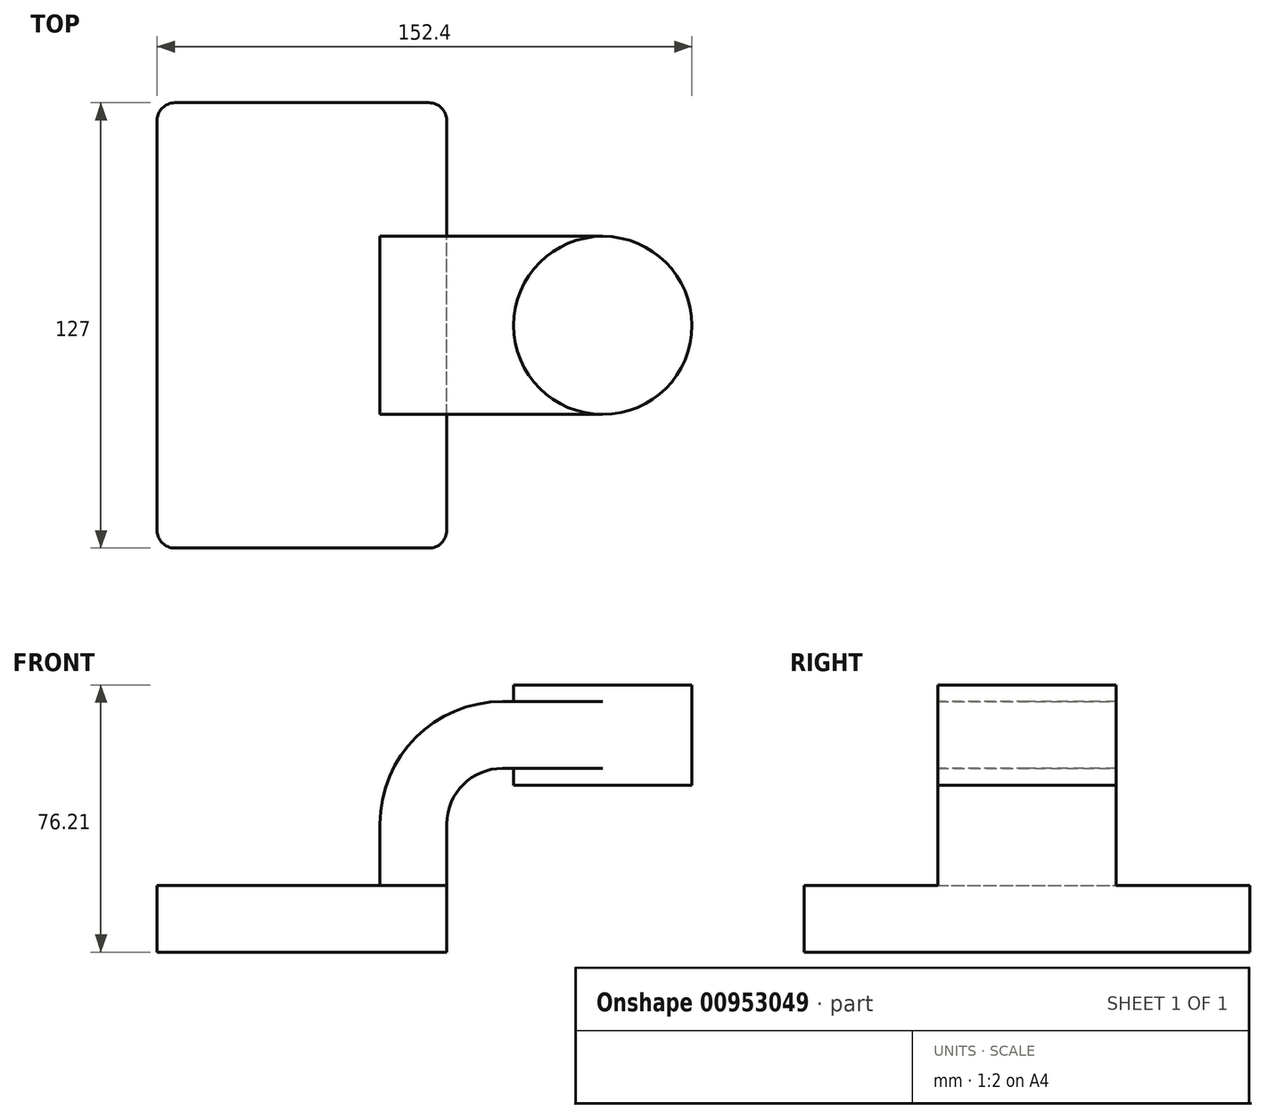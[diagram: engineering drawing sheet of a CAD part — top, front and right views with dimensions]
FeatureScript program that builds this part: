
annotation { "Feature Type Name" : "Feature", "Feature Type Description" : "" }
export const myFeature = defineFeature(function(context is Context, id is Id, definition is map)
    precondition{}
    {
        {
            var Q0;
            Q0=qCreatedBy(makeId("Front.planeOp"),FACE);
            var sketch = newSketch(context, id + "F0", { "sketchPlane" : qUnion([Q0])});
            skLineSegment(sketch, "E0.bottom", {"start": v(-41.28, 9.53) * mm, "end": v(41.28, 9.53) * mm});
            skLineSegment(sketch, "E0.top", {"start": v(-41.28, -9.53) * mm, "end": v(41.28, -9.53) * mm});
            skLineSegment(sketch, "E0.left", {"start": v(-41.28, 9.53) * mm, "end": v(-41.28, -9.53) * mm});
            skLineSegment(sketch, "E0.right", {"start": v(41.27, 9.53) * mm, "end": v(41.28, -9.53) * mm});
            skLineSegment(sketch, "E1.bottom", {"start": v(60.32, 66.68) * mm, "end": v(111.12, 66.68) * mm});
            skLineSegment(sketch, "E1.top", {"start": v(60.32, 38.1) * mm, "end": v(111.12, 38.1) * mm});
            skLineSegment(sketch, "E1.left", {"start": v(60.32, 66.68) * mm, "end": v(60.32, 38.1) * mm});
            skLineSegment(sketch, "E1.right", {"start": v(111.12, 66.68) * mm, "end": v(111.12, 38.1) * mm});
            skPoint(sketch, "E1.middle", {"position": v(85.72, 52.39) * mm});
            skLineSegment(sketch, "E2", {"start": v(41.27, 9.53) * mm, "end": v(41.27, 27) * mm});
            skArc(sketch, "E3", {"start": v(41.28, 27) * mm, "mid": v(45.92, 38.23) * mm, "end": v(57.15, 42.88) * mm});
            skLineSegment(sketch, "E4", {"start": v(57.15, 42.88) * mm, "end": v(85.72, 42.88) * mm});
            skLineSegment(sketch, "E5.0", {"start": v(57.15, 61.93) * mm, "end": v(85.72, 61.93) * mm});
            skArc(sketch, "E5.1", {"start": v(22.23, 27) * mm, "mid": v(32.45, 51.7) * mm, "end": v(57.15, 61.93) * mm});
            skLineSegment(sketch, "E5.2", {"start": v(22.23, 9.53) * mm, "end": v(22.23, 27) * mm});
            skLineSegment(sketch, "E6", {"start": v(85.72, 38.1) * mm, "end": v(85.72, 66.68) * mm});
            skFitSpline(sketch, "E7", {"points": [v(-41.28, 9.53) * mm, v(57.15, 61.93) * mm], "startDerivative": vector(2.38, 87.5) * mm, "endDerivative": vector(125.75, -2.56) * mm});
            skSolve(sketch);
        }
        {
            var Q0;
            Q0=makeQuery(id+"F0.imprint","IMPRINT",FACE,{"disambiguationData":[TD([[makeQuery(id+"F0.imprint","IMPRINT",EDGE,{"derivedFrom":sQuery(id+"F0.wireOp",EDGE,"E0.top")}),1.0]])]});
            extrude(context, id + "F1", {"entities" : qUnion([Q0]), "endBound" : BoundingType.SYMMETRIC, "depth" : 127 * mm, "offsetDistance" : 25.4 * mm});
        }
        {
            var Q0;
            {var subQ1=sQuery(id+"F0.wireOp",EDGE,"E2");Q0=makeQuery(id+"F0.imprint","IMPRINT",FACE,{"disambiguationData":[TD([[makeQuery(id+"F0.imprint","IMPRINT",EDGE,{"derivedFrom":subQ1}),1.0]])]});}
            var Q1;
            {var subQ0=sQuery(id+"F0.wireOp",EDGE,"E5.0");var subQ1=sQuery(id+"F0.wireOp",EDGE,"E1.left");var subQ2=makeQuery(id+"F0.imprint","INTERSECT",VERTEX,{"derivedFrom":[subQ1,subQ0]});Q1=makeQuery(id+"F0.imprint","IMPRINT",FACE,{"disambiguationData":[TD([[makeQuery(id+"F0.imprint","IMPRINT",EDGE,{"disambiguationData":[TD([[subQ2,-1.0]])],"derivedFrom":subQ1}),1.0]])]});}
            extrude(context, id + "F2", {"entities" : qUnion([Q0, Q1]), "operationType" : NewBodyOperationType.ADD, "endBound" : BoundingType.SYMMETRIC, "depth" : 50.8 * mm, "offsetDistance" : 25.4 * mm});
        }
        {
            var Q0;
            Q0=makeQuery(id+"F0.imprint","IMPRINT",FACE,{"disambiguationData":[TD([[makeQuery(id+"F0.imprint","IMPRINT",EDGE,{"derivedFrom":sQuery(id+"F0.wireOp",EDGE,"E5.1")}),1.0]])]});
            extrude(context, id + "F3", {"entities" : qUnion([Q0]), "operationType" : NewBodyOperationType.ADD, "endBound" : BoundingType.SYMMETRIC, "depth" : 15.88 * mm, "offsetDistance" : 25.4 * mm});
        }
        {
            var Q0;
            {var subQ0=sQuery(id+"F0.wireOp",EDGE,"E1.right");Q0=makeQuery(id+"F0.imprint","IMPRINT",FACE,{"disambiguationData":[TD([[makeQuery(id+"F0.imprint","IMPRINT",EDGE,{"derivedFrom":subQ0}),-1.0]])]});}
            var Q1;
            Q1=sQuery(id+"F0.wireOp",EDGE,"E6");
            revolve(context, id + "F4", {"operationType" : NewBodyOperationType.ADD, "surfaceOperationType" : NewSurfaceOperationType.NEW, "entities" : qUnion([Q0]), "axis" : qUnion([Q1]), "revolveType" : RevolveType.FULL});
        }
        {
            var Q0;
            Q0=makeQuery(id+"F1.opExtrude","CAP_EDGE",EDGE,{"disambiguationData":[OSD([sQuery(id+"F0.wireOp",EDGE,"E0.right")])],"isStart":true});
            var Q1;
            Q1=makeQuery(id+"F1.opExtrude","CAP_EDGE",EDGE,{"disambiguationData":[OSD([sQuery(id+"F0.wireOp",EDGE,"E0.left")])],"isStart":true});
            var Q2;
            Q2=makeQuery(id+"F1.opExtrude","CAP_EDGE",EDGE,{"disambiguationData":[OSD([sQuery(id+"F0.wireOp",EDGE,"E0.left")])],"isStart":false});
            var Q3;
            Q3=makeQuery(id+"F1.opExtrude","CAP_EDGE",EDGE,{"disambiguationData":[OSD([sQuery(id+"F0.wireOp",EDGE,"E0.right")])],"isStart":false});
            fillet(context, id + "F5", {"entities" : qUnion([Q0, Q1, Q2, Q3]), "radius" : 5.08 * mm, "tangentPropagation" : true, "allowEdgeOverflow" : false});
        }
    });
